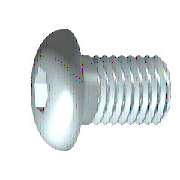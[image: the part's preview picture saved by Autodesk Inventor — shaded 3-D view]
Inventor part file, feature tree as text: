
AUTODESK INVENTOR PART (.ipt)
format: ipt  version: 2025 (Build 290162010, 162A)  size: 201,216 bytes
history: native  units: mm (DEFAULTED — no unit token found)
features: extrude x1, plane x1, fillet x1
ambient origin geometry x7: Origin, YZ Plane, XY Plane, X Axis, Y Axis, Z Axis, Center Point
bodies: Solid1 (feature_tree), Body (feature_tree)
feature tree (3):
  extrude  "Slot"  Depth=4.5mm
  plane  "Work Plane1"
  fillet  "Fillet2"  Radius=0.306825mm
